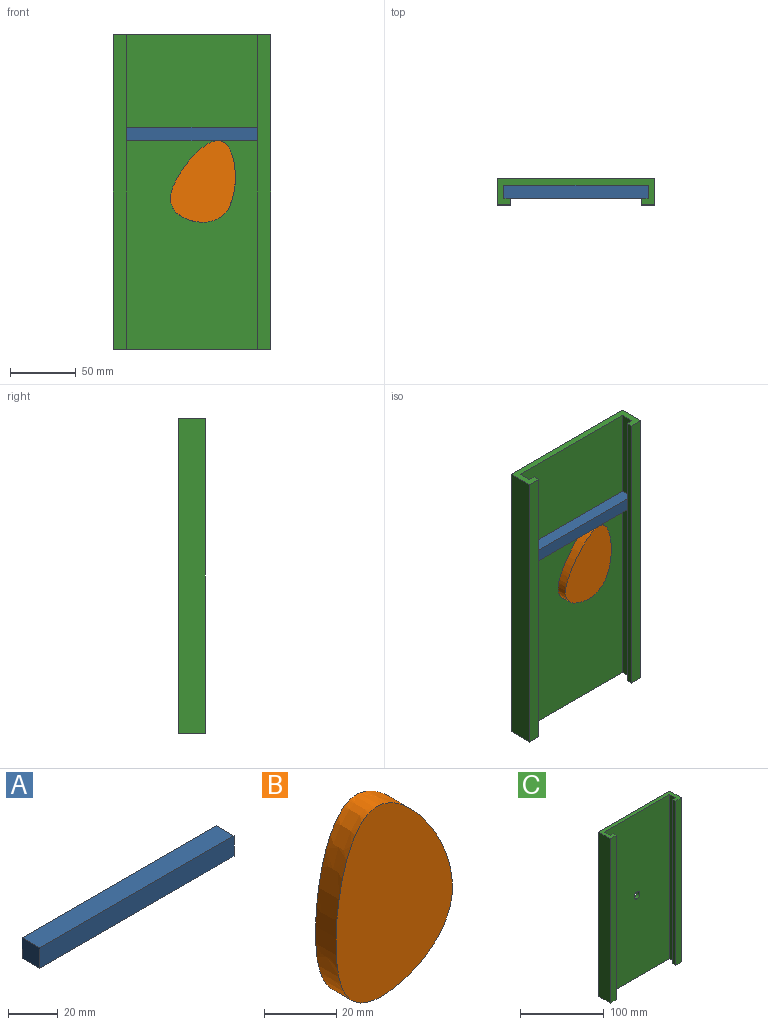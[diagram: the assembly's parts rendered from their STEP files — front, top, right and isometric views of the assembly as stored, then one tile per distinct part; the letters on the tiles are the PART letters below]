
ASSEMBLY  parts=3 mates=2
PART A: 6 faces, bbox 110x10x10 mm
  f0: plane 10x10mm, normal (1,0,0), area 100mm2, adj f1,f2,f4,f5
  f1: plane 110x10mm, normal (0,0,1), area 1100mm2, adj f0,f3,f4,f5
  f2: plane 110x10mm, normal (0,0,-1), area 1100mm2, adj f0,f3,f4,f5
  f3: plane 10x10mm, normal (-1,0,0), area 100mm2, adj f1,f2,f4,f5
  f4: plane 110x10mm, normal (0,1,0), area 1100mm2, adj f0,f1,f2,f3
  f5: plane 110x10mm, normal (0,-1,0), area 1100mm2, adj f0,f1,f2,f3
PART B: 5 faces, bbox 51x15x69 mm
  f0: plane 10x10mm, normal (0,1,0), area 78.5mm2, adj f1
  f1: cylinder r=5mm len=10mm, axis (0,-1,0), area 219.9mm2, adj f0,f4
  f2: extruded ~65.1x45.46mm, area 1405.8mm2, adj f3,f4
  f3: plane 69.02x51.05mm, normal (0,-1,0), area 2271.9mm2, adj f2
  f4: plane 69.02x51.05mm, normal (0,1,0), area 2193.4mm2, adj f1,f2
PART C: 15 faces, bbox 120x20x240 mm
  f0: plane 240x5mm, normal (1,0,0), area 1200mm2, adj f1,f3,f8,f13
  f1: plane 120x20mm, normal (0,0,-1), area 800mm2, adj f0,f2,f4,f5,f6,f7,f8,f9
  f2: plane 240x5mm, normal (-1,0,0), area 1200mm2, adj f1,f3,f6,f11
  f3: plane 120x20mm, normal (0,0,1), area 800mm2, adj f0,f2,f4,f5,f6,f7,f8,f9
  f4: plane 240x110mm, normal (0,-1,0), area 26321.5mm2, adj f1,f3,f5,f7,f14
  f5: plane 240x10mm, normal (-1,0,0), area 2400mm2, adj f1,f3,f4,f6
  f6: plane 240x5mm, normal (0,1,0), area 1200mm2, adj f1,f2,f3,f5
  f7: plane 240x10mm, normal (1,0,0), area 2400mm2, adj f1,f3,f4,f8
  f8: plane 240x5mm, normal (0,1,0), area 1200mm2, adj f0,f1,f3,f7
  f9: plane 240x120mm, normal (0,1,0), area 28721.5mm2, adj f1,f3,f10,f12,f14
  f10: plane 240x20mm, normal (1,0,0), area 4800mm2, adj f1,f3,f9,f11
  f11: plane 240x10mm, normal (0,-1,0), area 2400mm2, adj f1,f2,f3,f10
  f12: plane 240x20mm, normal (-1,0,0), area 4800mm2, adj f1,f3,f9,f13
  f13: plane 240x10mm, normal (0,-1,0), area 2400mm2, adj f0,f1,f3,f12
  f14: cylinder r=5mm len=10mm, axis (0,-1,0), area 157.1mm2, adj f4,f9
PLACE A t=(0,0,-70.79)mm
PLACE B rot(axis=(0,1,0),31.4deg) t=(-102.38,0,62.6)mm
PLACE C at identity fixed
MATE slider C.f3 <-> A.f1  axis (0,0,1) through (-55,2,120)mm
MATE revolute C.f14 <-> B.f1  axis (0,1,0) through (0,7,0)mm
